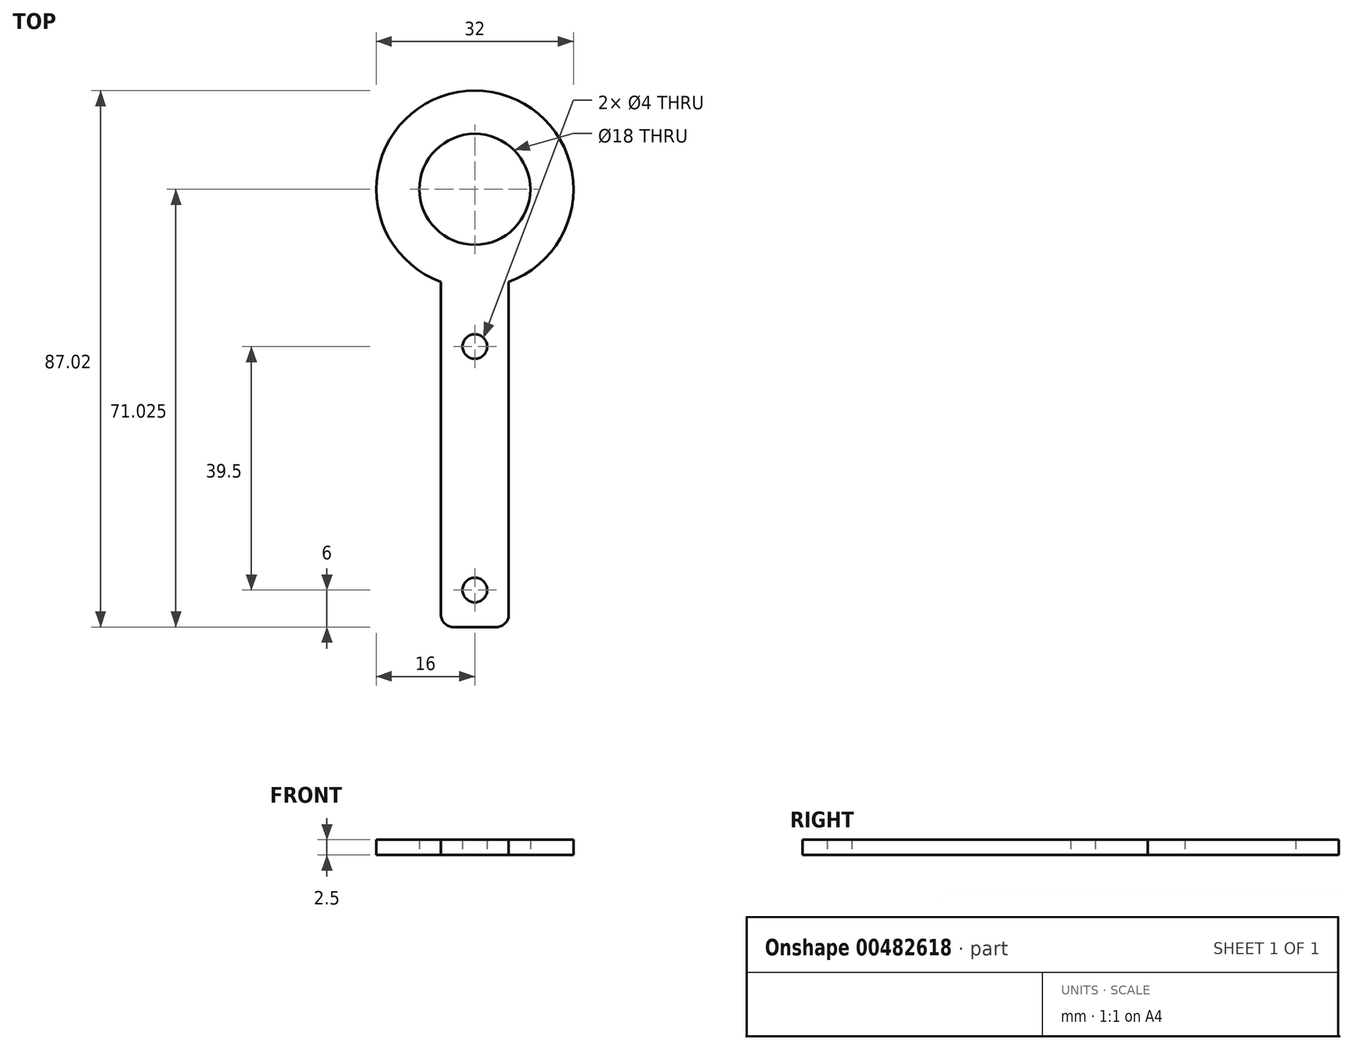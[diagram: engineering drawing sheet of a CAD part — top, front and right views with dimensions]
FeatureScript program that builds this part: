
annotation { "Feature Type Name" : "Feature", "Feature Type Description" : "" }
export const myFeature = defineFeature(function(context is Context, id is Id, definition is map)
    precondition{}
    {
        {
            var Q0;
            Q0=qCreatedBy(makeId("Top.planeOp"),FACE);
            var sketch = newSketch(context, id + "F0", { "sketchPlane" : qUnion([Q0])});
            skLineSegment(sketch, "E0", {"start": v(2, 0) * mm, "end": v(9, 0) * mm});
            skLineSegment(sketch, "E1", {"start": v(11, 2) * mm, "end": v(11, 56) * mm});
            skLineSegment(sketch, "E2", {"start": v(0, 56) * mm, "end": v(0, 2) * mm});
            skArc(sketch, "E3", {"start": v(11, 56) * mm, "mid": v(5.5, 87.02) * mm, "end": v(0, 56) * mm});
            skCircle(sketch, "E4", {"center": v(5.5, 71.02) * mm, "radius": 9 * mm});
            skCircle(sketch, "E5", {"center": v(5.5, 6) * mm, "radius": 2 * mm});
            skCircle(sketch, "E6", {"center": v(5.5, 45.5) * mm, "radius": 2 * mm});
            skLineSegment(sketch, "E7", {"start": v(5.5, 0) * mm, "end": v(5.5, 97.78) * mm, "construction": true});
            skPoint(sketch, "E8.visualSharp", {"position": v(0, 0) * mm});
            skArc(sketch, "E8.filletArc", {"start": v(0, 2) * mm, "mid": v(0.59, 0.59) * mm, "end": v(2, 0) * mm});
            skPoint(sketch, "E9.visualSharp", {"position": v(11, 0) * mm});
            skArc(sketch, "E9.filletArc", {"start": v(9, 0) * mm, "mid": v(10.41, 0.59) * mm, "end": v(11, 2) * mm});
            skSolve(sketch);
        }
        {
            var Q0;
            Q0 = qSketchRegion(id + "F0", true);
            extrude(context, id + "F1", {"entities" : qUnion([Q0]), "depth" : 2.5 * mm});
        }
    });
